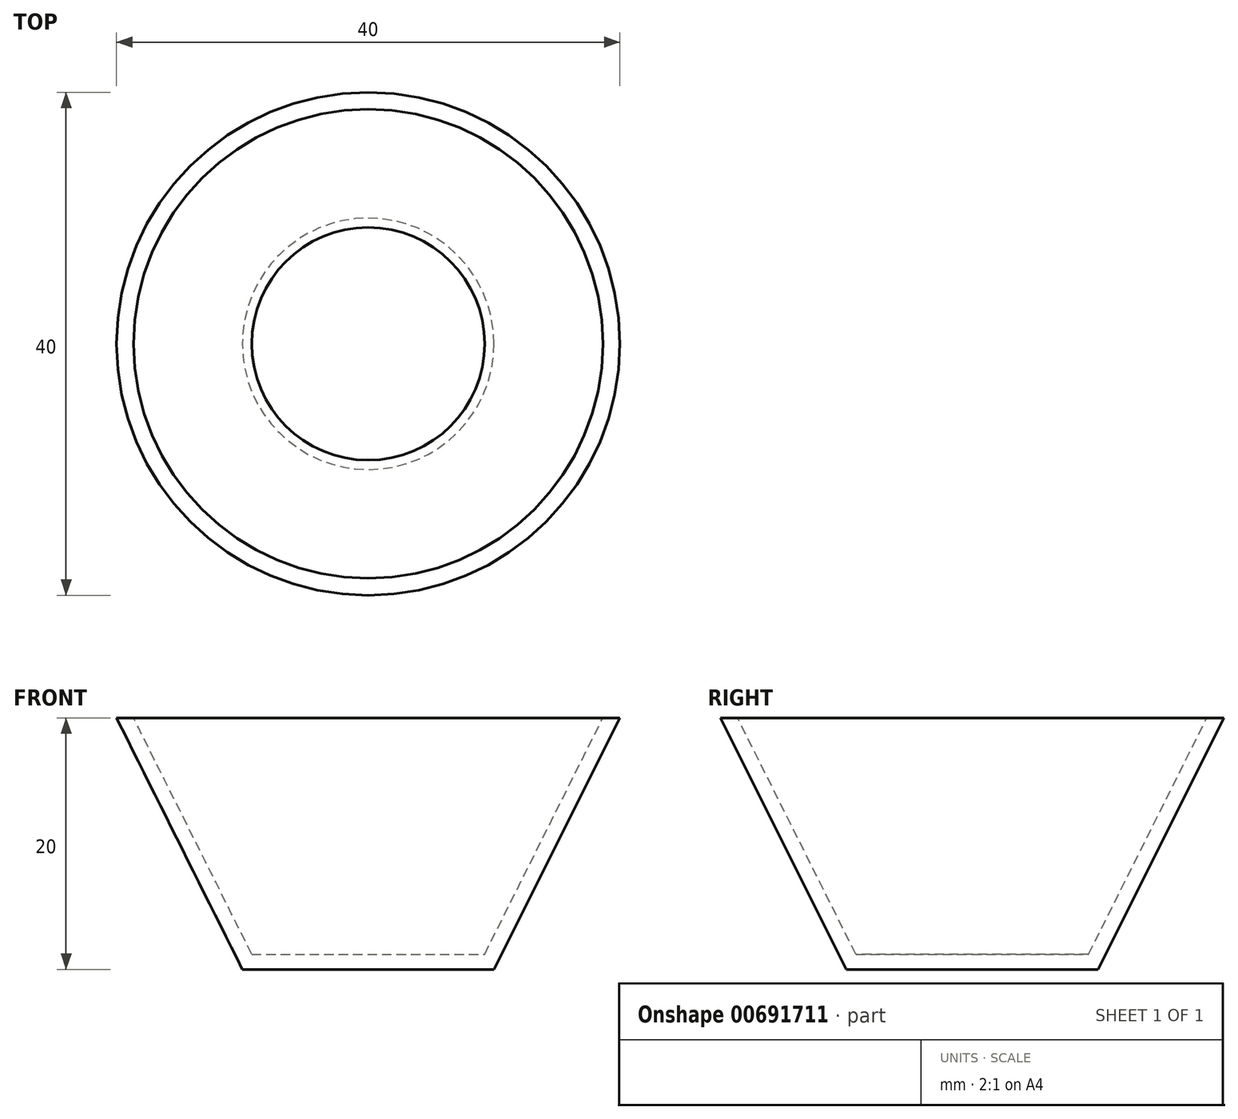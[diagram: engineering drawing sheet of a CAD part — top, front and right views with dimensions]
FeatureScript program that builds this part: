
annotation { "Feature Type Name" : "Feature", "Feature Type Description" : "" }
export const myFeature = defineFeature(function(context is Context, id is Id, definition is map)
    precondition{}
    {
        {
            var Q0;
            Q0=qCreatedBy(makeId("Front.planeOp"),FACE);
            var sketch = newSketch(context, id + "F0", { "sketchPlane" : qUnion([Q0])});
            skLineSegment(sketch, "E0", {"start": v(0, 0) * mm, "end": v(0, 20) * mm, "construction": true});
            skLineSegment(sketch, "E1", {"start": v(0, 0) * mm, "end": v(10, 0) * mm});
            skLineSegment(sketch, "E2", {"start": v(10, 0) * mm, "end": v(20, 20) * mm});
            skLineSegment(sketch, "E3.0", {"start": v(9.25, 1.2) * mm, "end": v(18.65, 20) * mm});
            skLineSegment(sketch, "E3.1", {"start": v(0, 1.21) * mm, "end": v(9.25, 1.21) * mm});
            skLineSegment(sketch, "E4", {"start": v(18.65, 20) * mm, "end": v(20, 20) * mm});
            skLineSegment(sketch, "E5", {"start": v(0, 1.21) * mm, "end": v(0, 0) * mm});
            skSolve(sketch);
        }
        {
            var Q0;
            Q0=makeQuery(id+"F0.imprint","IMPRINT",FACE,{"disambiguationData":[TD([[makeQuery(id+"F0.imprint","IMPRINT",EDGE,{"derivedFrom":sQuery(id+"F0.wireOp",EDGE,"E1")}),1.0]])]});
            var Q1;
            Q1=sQuery(id+"F0.wireOp",EDGE,"E0");
            revolve(context, id + "F1", {"entities" : qUnion([Q0]), "axis" : qUnion([Q1]), "revolveType" : RevolveType.FULL});
        }
    });
